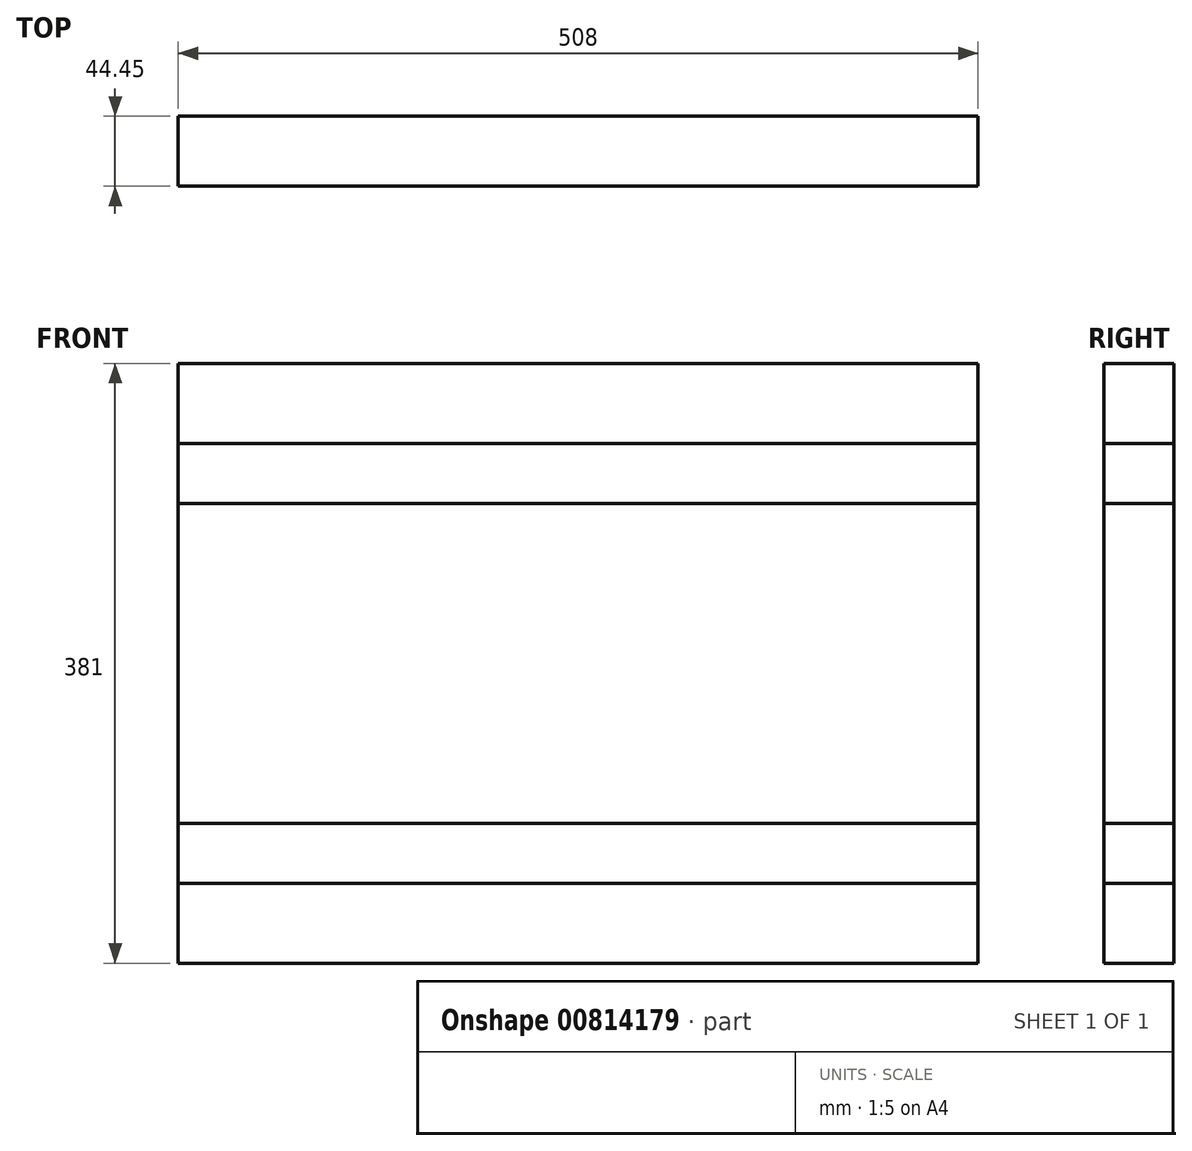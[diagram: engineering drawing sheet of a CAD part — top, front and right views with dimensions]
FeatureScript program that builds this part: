
annotation { "Feature Type Name" : "Feature", "Feature Type Description" : "" }
export const myFeature = defineFeature(function(context is Context, id is Id, definition is map)
    precondition{}
    {
        {
            var Q0;
            Q0=qCreatedBy(makeId("Front.planeOp"),FACE);
            var sketch = newSketch(context, id + "F0", { "sketchPlane" : qUnion([Q0])});
            skLineSegment(sketch, "E0.bottom", {"start": v(-158.98, 156.96) * mm, "end": v(349.02, 156.96) * mm});
            skLineSegment(sketch, "E0.top", {"start": v(-158.98, -224.04) * mm, "end": v(349.02, -224.04) * mm});
            skLineSegment(sketch, "E0.left", {"start": v(-158.98, 156.96) * mm, "end": v(-158.98, -224.04) * mm});
            skLineSegment(sketch, "E0.right", {"start": v(349.02, 156.96) * mm, "end": v(349.02, -224.04) * mm});
            skLineSegment(sketch, "E1.bottom", {"start": v(-158.98, 106.16) * mm, "end": v(349.02, 106.16) * mm});
            skLineSegment(sketch, "E1.top", {"start": v(-158.98, 68.06) * mm, "end": v(349.02, 68.06) * mm});
            skLineSegment(sketch, "E1.left", {"start": v(-158.98, 106.16) * mm, "end": v(-158.98, 68.06) * mm});
            skLineSegment(sketch, "E1.right", {"start": v(349.02, 106.16) * mm, "end": v(349.02, 68.06) * mm});
            skLineSegment(sketch, "E2.bottom", {"start": v(-158.98, -135.14) * mm, "end": v(349.02, -135.14) * mm});
            skLineSegment(sketch, "E2.top", {"start": v(-158.98, -173.24) * mm, "end": v(349.02, -173.24) * mm});
            skLineSegment(sketch, "E2.left", {"start": v(-158.98, -135.14) * mm, "end": v(-158.98, -173.24) * mm});
            skLineSegment(sketch, "E2.right", {"start": v(349.02, -135.14) * mm, "end": v(349.02, -173.24) * mm});
            skSolve(sketch);
        }
        {
            var Q0;
            Q0=makeQuery(id+"F0.imprint","IMPRINT",FACE,{"disambiguationData":[TD([[makeQuery(id+"F0.imprint","IMPRINT",EDGE,{"derivedFrom":sQuery(id+"F0.wireOp",EDGE,"E1.bottom")}),-1.0]])]});
            extrude(context, id + "F1", {"entities" : qUnion([Q0]), "depth" : 44.45 * mm, "offsetDistance" : 25.4 * mm});
        }
        {
            var Q0;
            Q0=makeQuery(id+"F0.imprint","IMPRINT",FACE,{"disambiguationData":[TD([[makeQuery(id+"F0.imprint","IMPRINT",EDGE,{"derivedFrom":sQuery(id+"F0.wireOp",EDGE,"E2.bottom")}),-1.0]])]});
            extrude(context, id + "F2", {"entities" : qUnion([Q0]), "depth" : 44.45 * mm, "offsetDistance" : 25.4 * mm});
        }
        {
            var Q0;
            {var subQ0=sQuery(id+"F0.wireOp",EDGE,"E1.top");Q0=makeQuery(id+"F0.imprint","IMPRINT",FACE,{"disambiguationData":[TD([[makeQuery(id+"F0.imprint","IMPRINT",EDGE,{"derivedFrom":subQ0}),-1.0]])]});}
            var Q1;
            {var subQ0=sQuery(id+"F0.wireOp",EDGE,"E0.bottom");Q1=makeQuery(id+"F0.imprint","IMPRINT",FACE,{"disambiguationData":[TD([[makeQuery(id+"F0.imprint","IMPRINT",EDGE,{"derivedFrom":subQ0}),-1.0]])]});}
            var Q2;
            {var subQ0=sQuery(id+"F0.wireOp",EDGE,"E0.top");Q2=makeQuery(id+"F0.imprint","IMPRINT",FACE,{"disambiguationData":[TD([[makeQuery(id+"F0.imprint","IMPRINT",EDGE,{"derivedFrom":subQ0}),1.0]])]});}
            extrude(context, id + "F3", {"entities" : qUnion([Q0, Q1, Q2]), "depth" : 44.45 * mm, "offsetDistance" : 25.4 * mm});
        }
    });
